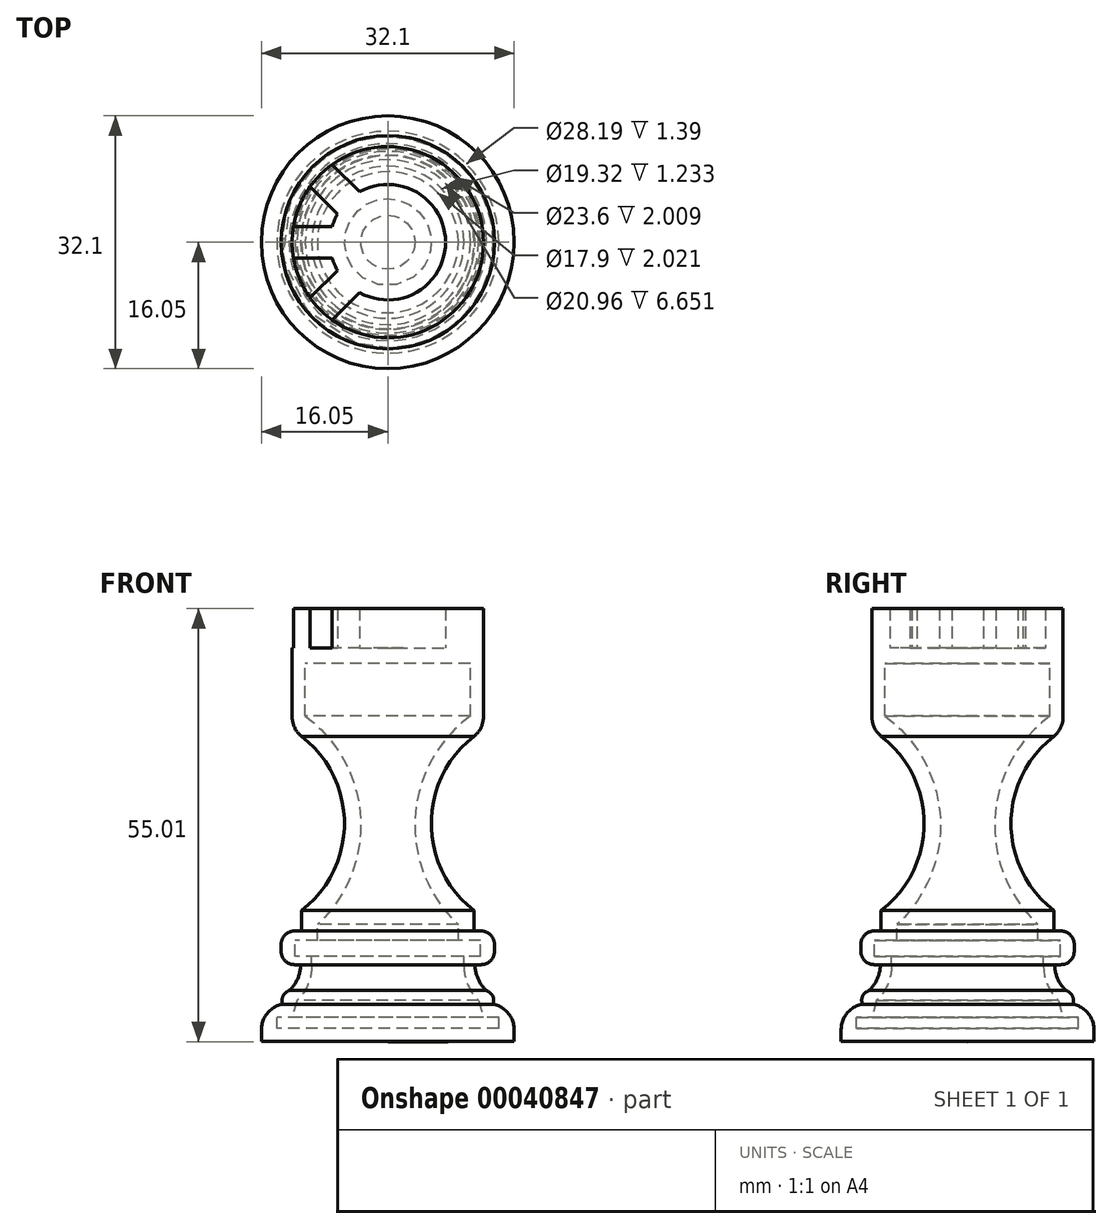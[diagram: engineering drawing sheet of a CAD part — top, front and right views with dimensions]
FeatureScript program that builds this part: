
annotation { "Feature Type Name" : "Feature", "Feature Type Description" : "" }
export const myFeature = defineFeature(function(context is Context, id is Id, definition is map)
    precondition{}
    {
        {
            var Q0;
            Q0=qCreatedBy(makeId("Front.planeOp"),FACE);
            var sketch = newSketch(context, id + "F0", { "sketchPlane" : qUnion([Q0]), "disableImprinting" : false});
            skLineSegment(sketch, "E0", {"start": v(0, -20.1) * mm, "end": v(-2, -20.1) * mm});
            skLineSegment(sketch, "E1", {"start": v(-2, 29.91) * mm, "end": v(-12.14, 29.91) * mm});
            skLineSegment(sketch, "E2", {"start": v(-12.14, 29.91) * mm, "end": v(-12.14, 21.17) * mm});
            skArc(sketch, "E3", {"start": v(-12.14, 21.17) * mm, "mid": v(-11.84, 19.8) * mm, "end": v(-10.97, 18.7) * mm});
            skArc(sketch, "E4", {"start": v(-10.97, -3.45) * mm, "mid": v(-5.51, 7.62) * mm, "end": v(-10.97, 18.7) * mm});
            skLineSegment(sketch, "E5", {"start": v(-10.97, -3.45) * mm, "end": v(-10.97, -6.04) * mm});
            skLineSegment(sketch, "E6", {"start": v(-10.97, -6.04) * mm, "end": v(-13.55, -6.04) * mm});
            skLineSegment(sketch, "E7", {"start": v(-13.55, -6.04) * mm, "end": v(-13.55, -10.32) * mm});
            skLineSegment(sketch, "E8", {"start": v(-13.55, -10.32) * mm, "end": v(-11.08, -10.32) * mm});
            skArc(sketch, "E9", {"start": v(-12.52, -13.62) * mm, "mid": v(-11.46, -12.12) * mm, "end": v(-11.08, -10.32) * mm});
            skArc(sketch, "E10", {"start": v(-12.52, -13.62) * mm, "mid": v(-13.32, -14.3) * mm, "end": v(-13.36, -15.33) * mm});
            skLineSegment(sketch, "E11", {"start": v(-13.36, -15.33) * mm, "end": v(-16.05, -15.33) * mm});
            skLineSegment(sketch, "E12", {"start": v(-2, -20.1) * mm, "end": v(-16.05, -20.09) * mm});
            skLineSegment(sketch, "E13", {"start": v(-16.05, -20.09) * mm, "end": v(-16.05, -15.33) * mm});
            skLineSegment(sketch, "E14", {"start": v(-2, 29.91) * mm, "end": v(0, 29.9) * mm});
            skLineSegment(sketch, "E15", {"start": v(0, 27.91) * mm, "end": v(-10.48, 27.91) * mm});
            skLineSegment(sketch, "E16", {"start": v(-10.48, 27.91) * mm, "end": v(-10.48, 21.26) * mm});
            skArc(sketch, "E17", {"start": v(-8.95, -5.21) * mm, "mid": v(-3.47, 8.38) * mm, "end": v(-10.48, 21.26) * mm});
            skLineSegment(sketch, "E18", {"start": v(-8.95, -5.21) * mm, "end": v(-8.95, -7.24) * mm});
            skLineSegment(sketch, "E19", {"start": v(-8.95, -7.24) * mm, "end": v(-11.8, -7.24) * mm});
            skLineSegment(sketch, "E20", {"start": v(-11.8, -7.24) * mm, "end": v(-11.8, -9.24) * mm});
            skLineSegment(sketch, "E21", {"start": v(-11.8, -9.24) * mm, "end": v(-9.66, -9.24) * mm});
            skLineSegment(sketch, "E22", {"start": v(-9.66, -9.24) * mm, "end": v(-9.66, -10.48) * mm});
            skLineSegment(sketch, "E23", {"start": v(-12.15, -17.04) * mm, "end": v(-14.1, -17.04) * mm});
            skLineSegment(sketch, "E24", {"start": v(-14.1, -17.04) * mm, "end": v(-14.1, -18.43) * mm});
            skLineSegment(sketch, "E25", {"start": v(-14.1, -18.43) * mm, "end": v(0, -18.43) * mm});
            skLineSegment(sketch, "E26", {"start": v(0, -18.43) * mm, "end": v(0, -20.1) * mm});
            skLineSegment(sketch, "E27", {"start": v(0, 29.9) * mm, "end": v(0, 27.91) * mm});
            skLineSegment(sketch, "E28", {"start": v(-12.15, -17.04) * mm, "end": v(-11.54, -14.86) * mm});
            skArc(sketch, "E29", {"start": v(-11.54, -14.86) * mm, "mid": v(-10.15, -12.86) * mm, "end": v(-9.66, -10.48) * mm});
            skSolve(sketch);
        }
        {
            var Q0;
            Q0=makeQuery(id+"F0.imprint","IMPRINT",FACE,{"disambiguationData":[TD([[makeQuery(id+"F0.imprint","IMPRINT",EDGE,{"derivedFrom":sQuery(id+"F0.wireOp",EDGE,"E0")}),-1.0]])]});
            var Q1;
            Q1=sQuery(id+"F0.wireOp",EDGE,"E27");
            revolve(context, id + "F1", {"surfaceOperationType" : NewSurfaceOperationType.NEW, "entities" : qUnion([Q0]), "axis" : qUnion([Q1]), "revolveType" : RevolveType.FULL});
        }
        {
            var Q0;
            Q0=makeQuery(id+"F1.opRevolve","SWEPT_EDGE",EDGE,{"disambiguationData":[OSD([sQuery(id+"F0.wireOp",EDGE,"E6"),sQuery(id+"F0.wireOp",EDGE,"E7")])]});
            var Q1;
            Q1=makeQuery(id+"F1.opRevolve","SWEPT_EDGE",EDGE,{"disambiguationData":[OSD([sQuery(id+"F0.wireOp",EDGE,"E7"),sQuery(id+"F0.wireOp",EDGE,"E8")])]});
            fillet(context, id + "F2", {"entities" : qUnion([Q0, Q1]), "radius" : 1.71 * mm, "tangentPropagation" : true, "allowEdgeOverflow" : false});
        }
        {
            var Q0;
            Q0=makeQuery(id+"F1.opRevolve","SWEPT_EDGE",EDGE,{"disambiguationData":[OSD([sQuery(id+"F0.wireOp",EDGE,"E11"),sQuery(id+"F0.wireOp",EDGE,"E13")])]});
            fillet(context, id + "F3", {"entities" : qUnion([Q0]), "radius" : 3.3 * mm, "tangentPropagation" : true, "allowEdgeOverflow" : false});
        }
        {
            var Q0;
            Q0=makeQuery(id+"F1.opRevolve","SWEPT_FACE",FACE,{"disambiguationData":[OSD([sQuery(id+"F0.wireOp",EDGE,"E1"),sQuery(id+"F0.wireOp",EDGE,"E14")])]});
            var sketch = newSketch(context, id + "F4", { "sketchPlane" : qUnion([Q0])});
            skLineSegment(sketch, "E30", {"start": v(-2, 7.06) * mm, "end": v(-2, 4.83) * mm});
            skLineSegment(sketch, "E31", {"start": v(11.98, -2) * mm, "end": v(4.83, -2) * mm});
            skLineSegment(sketch, "E32", {"start": v(11.98, 2) * mm, "end": v(4.83, 2) * mm});
            skLineSegment(sketch, "E33", {"start": v(0, 2) * mm, "end": v(-2, 0) * mm});
            skLineSegment(sketch, "E34", {"start": v(-1, 1) * mm, "end": v(0, 2) * mm});
            skLineSegment(sketch, "E35", {"start": v(0, -2) * mm, "end": v(2, 0) * mm});
            skLineSegment(sketch, "E36", {"start": v(2, 0) * mm, "end": v(0, -2) * mm});
            skLineSegment(sketch, "E37", {"start": v(2, 0) * mm, "end": v(0, 2) * mm});
            skLineSegment(sketch, "E38", {"start": v(0, 2) * mm, "end": v(2, 0) * mm});
            skLineSegment(sketch, "E39", {"start": v(-2, 0) * mm, "end": v(0, -2) * mm});
            skLineSegment(sketch, "E40", {"start": v(0, -2) * mm, "end": v(-2, 0) * mm});
            skLineSegment(sketch, "E41.trimOffspring", {"start": v(-2, -4.83) * mm, "end": v(-2, -7.06) * mm});
            skLineSegment(sketch, "E42.trimOffspring", {"start": v(2, -4.83) * mm, "end": v(2, -11.98) * mm});
            skLineSegment(sketch, "E43.trimOffspring", {"start": v(4.83, -2) * mm, "end": v(11.98, -2) * mm});
            skLineSegment(sketch, "E44.trimOffspring", {"start": v(2, 4.83) * mm, "end": v(2, 11.98) * mm});
            skLineSegment(sketch, "E45.trimOffspring", {"start": v(4.83, 2) * mm, "end": v(11.98, 2) * mm});
            skLineSegment(sketch, "E46.trimOffspring", {"start": v(-4.83, 2) * mm, "end": v(-7.06, 2) * mm});
            skLineSegment(sketch, "E47.trimOffspring", {"start": v(-4.83, -2) * mm, "end": v(-7.06, -2) * mm});
            skLineSegment(sketch, "E48", {"start": v(0, 0) * mm, "end": v(1, -1) * mm});
            skLineSegment(sketch, "E49", {"start": v(0.8, -0.8) * mm, "end": v(1.41, -1.41) * mm});
            skLineSegment(sketch, "E50", {"start": v(0.34, -0.34) * mm, "end": v(-1.41, 1.41) * mm});
            skLineSegment(sketch, "E51", {"start": v(1.41, -1.41) * mm, "end": v(2.83, 0) * mm});
            skLineSegment(sketch, "E52", {"start": v(1.41, -1.41) * mm, "end": v(0, -2.83) * mm});
            skLineSegment(sketch, "E53", {"start": v(-1.41, 1.41) * mm, "end": v(0, 2.83) * mm});
            skLineSegment(sketch, "E54", {"start": v(-1.41, 1.41) * mm, "end": v(-1, 1) * mm});
            skLineSegment(sketch, "E55", {"start": v(-1.41, 1.41) * mm, "end": v(-2.83, 0) * mm});
            skLineSegment(sketch, "E56", {"start": v(0, 0) * mm, "end": v(1.41, 1.41) * mm});
            skLineSegment(sketch, "E57", {"start": v(0, 0) * mm, "end": v(-1.41, -1.41) * mm});
            skLineSegment(sketch, "E58", {"start": v(1.41, 1.41) * mm, "end": v(2.83, 0) * mm});
            skLineSegment(sketch, "E59", {"start": v(1.41, 1.41) * mm, "end": v(0, 2.83) * mm});
            skLineSegment(sketch, "E60", {"start": v(-1.41, -1.41) * mm, "end": v(0, -2.83) * mm});
            skLineSegment(sketch, "E61", {"start": v(-1.41, -1.41) * mm, "end": v(-2.83, 0) * mm});
            skLineSegment(sketch, "E62.trimOffspring", {"start": v(-4.83, 2) * mm, "end": v(-6.4, 3.58) * mm});
            skLineSegment(sketch, "E63.trimOffspring", {"start": v(-4.83, -2) * mm, "end": v(-6.4, -3.58) * mm});
            skLineSegment(sketch, "E64.trimOffspring", {"start": v(-2, -4.83) * mm, "end": v(-3.58, -6.4) * mm});
            skLineSegment(sketch, "E65.trimOffspring", {"start": v(2, -4.83) * mm, "end": v(7.06, -9.88) * mm});
            skLineSegment(sketch, "E66.trimOffspring", {"start": v(4.83, -2) * mm, "end": v(9.88, -7.05) * mm});
            skLineSegment(sketch, "E67.trimOffspring", {"start": v(4.83, 2) * mm, "end": v(9.88, 7.05) * mm});
            skLineSegment(sketch, "E68.trimOffspring", {"start": v(2, 4.83) * mm, "end": v(7.06, 9.88) * mm});
            skLineSegment(sketch, "E69.trimOffspring", {"start": v(-2, 4.83) * mm, "end": v(-3.58, 6.4) * mm});
            skCircle(sketch, "E70", {"center": v(0, 0) * mm, "radius": 7.33 * mm});
            skCircle(sketch, "E71", {"center": v(0, 0) * mm, "radius": 2 * mm});
            skLineSegment(sketch, "E72", {"start": v(-2, -7.06) * mm, "end": v(-2, -11.98) * mm});
            skLineSegment(sketch, "E73", {"start": v(-3.58, -6.4) * mm, "end": v(-7.05, -9.88) * mm});
            skLineSegment(sketch, "E74", {"start": v(-6.4, -3.58) * mm, "end": v(-9.88, -7.06) * mm});
            skLineSegment(sketch, "E75", {"start": v(-7.06, -2) * mm, "end": v(-11.98, -2) * mm});
            skLineSegment(sketch, "E76", {"start": v(-7.06, 2) * mm, "end": v(-11.98, 2) * mm});
            skLineSegment(sketch, "E77", {"start": v(-6.4, 3.58) * mm, "end": v(-9.88, 7.05) * mm});
            skLineSegment(sketch, "E78", {"start": v(-3.58, 6.4) * mm, "end": v(-7.05, 9.88) * mm});
            skLineSegment(sketch, "E79", {"start": v(-2, 7.06) * mm, "end": v(-2, 11.98) * mm});
            skSolve(sketch);
        }
        {
            var Q0;
            {var subQ3=sQuery(id+"F4.wireOp",EDGE,"E44.trimOffspring");var subQ5=sQuery(id+"F4.wireOp",EDGE,"E70");var subQ7=makeQuery(id+"F4.imprint","INTERSECT",VERTEX,{"derivedFrom":[subQ3,subQ5]});Q0=makeQuery(id+"F4.imprint","IMPRINT",FACE,{"disambiguationData":[TD([[makeQuery(id+"F4.imprint","IMPRINT",EDGE,{"disambiguationData":[TD([[subQ7,1.0]])],"derivedFrom":subQ5}),-1.0]])]});}
            var Q1;
            {var subQ0=sQuery(id+"F4.wireOp",EDGE,"E70");var subQ3=sQuery(id+"F4.wireOp",EDGE,"E45.trimOffspring");var subQ4=makeQuery(id+"F4.imprint","INTERSECT",VERTEX,{"derivedFrom":[subQ3,subQ0]});Q1=makeQuery(id+"F4.imprint","IMPRINT",FACE,{"disambiguationData":[TD([[makeQuery(id+"F4.imprint","IMPRINT",EDGE,{"disambiguationData":[TD([[subQ4,-1.0]])],"derivedFrom":subQ0}),-1.0]])]});}
            var Q2;
            {var subQ3=sQuery(id+"F4.wireOp",EDGE,"E43.trimOffspring");var subQ5=sQuery(id+"F4.wireOp",EDGE,"E70");var subQ7=makeQuery(id+"F4.imprint","INTERSECT",VERTEX,{"derivedFrom":[subQ3,subQ5]});Q2=makeQuery(id+"F4.imprint","IMPRINT",FACE,{"disambiguationData":[TD([[makeQuery(id+"F4.imprint","IMPRINT",EDGE,{"disambiguationData":[TD([[subQ7,1.0]])],"derivedFrom":subQ5}),-1.0]])]});}
            var Q3;
            {var subQ3=sQuery(id+"F4.wireOp",EDGE,"E42.trimOffspring");var subQ5=sQuery(id+"F4.wireOp",EDGE,"E70");var subQ7=makeQuery(id+"F4.imprint","INTERSECT",VERTEX,{"derivedFrom":[subQ3,subQ5]});Q3=makeQuery(id+"F4.imprint","IMPRINT",FACE,{"disambiguationData":[TD([[makeQuery(id+"F4.imprint","IMPRINT",EDGE,{"disambiguationData":[TD([[subQ7,-1.0]])],"derivedFrom":subQ5}),-1.0]])]});}
            var Q4;
            {var subQ2=sQuery(id+"F4.wireOp",EDGE,"E78");Q4=makeQuery(id+"F4.imprint","IMPRINT",FACE,{"disambiguationData":[TD([[makeQuery(id+"F4.imprint","IMPRINT",EDGE,{"derivedFrom":subQ2}),-1.0]])]});}
            var Q5;
            {var subQ2=sQuery(id+"F4.wireOp",EDGE,"E76");Q5=makeQuery(id+"F4.imprint","IMPRINT",FACE,{"disambiguationData":[TD([[makeQuery(id+"F4.imprint","IMPRINT",EDGE,{"derivedFrom":subQ2}),-1.0]])]});}
            var Q6;
            {var subQ2=sQuery(id+"F4.wireOp",EDGE,"E74");Q6=makeQuery(id+"F4.imprint","IMPRINT",FACE,{"disambiguationData":[TD([[makeQuery(id+"F4.imprint","IMPRINT",EDGE,{"derivedFrom":subQ2}),-1.0]])]});}
            var Q7;
            {var subQ2=sQuery(id+"F4.wireOp",EDGE,"E72");Q7=makeQuery(id+"F4.imprint","IMPRINT",FACE,{"disambiguationData":[TD([[makeQuery(id+"F4.imprint","IMPRINT",EDGE,{"derivedFrom":subQ2}),-1.0]])]});}
            extrude(context, id + "F5", {"entities" : qUnion([Q0, Q1, Q2, Q3, Q4, Q5, Q6, Q7]), "operationType" : NewBodyOperationType.ADD, "depth" : 5 * mm});
        }
    });
